# Revit family: Civil_Drainage_ACO_StormBrixx wm
name_source: partatom
category: Pipe Accessories
revit_build: Autodesk Revit 2013 (Build: 20120221_2030(x64)
units: mm (PartAtom-declared; Revit-internal decimal feet)

## types (2) — shared parameters
Assembly Code = D2090300
Con A Out = 128 mm
Con B Out = 128 mm
Conection IN Dia = 225 mm  [stored 0.738189 ft]
Connection IN Rad = 113 mm
Connection OUT Dia = 225 mm  [stored 0.738189 ft]
Connection OUT Rad = 113 mm
Draindown Depth = 610 mm  [stored 2.00131 ft]
Draindown Width = 600 mm  [stored 1.9685 ft]
Exc A = 25.00°
Fax = +44 (0)1462 815895
Inlet Connection Pipe = Yes
Installation Guidelines = http://www.aco.co.uk
Keynote = R17:315
Layer Connector = Product Code: 314023, Material: Recycled Polypropylene, Weight: 0.1kg, Colour: Red, Dimensions: 100mm x 40mm x 46mm (L x W x H)
Location of ConIn = 900 mm  [stored 2.95276 ft]
Loss Method = K Coefficient from Table
Maintenance Guidelines = http://www.aco.co.uk
Manufacturer = ACO Technologies plc
Model = StormBrixx
Product Documentation = http://www.aco.co.uk
Product Website = www.stormbrixx.co.uk
Side Panel = Product Code: 314021, Material: Recycled Polypropylene, Weight: 1.6kg, Colour: Black, Dimensions: 580mm x 578mm x 35mm (L x W x H)
Tank Body = Product Code: 314020, Material: Recycled Polypropylene, Weight: 10kg, Colour: Black, Dimensions: 1200mm x 600mm x 305mm (L x W x H), Vertical compressive strength: 420 kN/m², Lateral compressive strength: 90 kN/m², Void Ratio: 95%
Telephone = +44 (0)1462 816666
Trap W = 600 mm  [stored 1.9685 ft]
URL = www.aco.co.uk
_current revision = 1
_distributed by = www.aco.co.uk
zero-valued in all types: Barcode, Cost, ExpectedLife, SerialNumber, TagNumber

## per-type parameters (varying)
| type | Description | MIC | Outlet Connection Pipe | Outlet Connection Side | SIC | Top Cover | Type Comments |
| Attenuation System Configuration | ACO StormBrixx Attenuation System, configured as Attenuation system | No | Yes | No | Yes | Product Code: 314022 (set of 4), Material: Recycled Polypropylene, Weight: 0.8kg (per set), Colour: Black, Dimensions: 550mm x550mm x 43mm (L x W x H) | Attenuation System |
| Infiltration System Configuration | ACO StormBrixx Auttenuation System, configured as Infiltration system | Yes | No | Yes | No | Product Code: 314022 (set of 4), Material: Recycled Polypropylene, Weight: 0.8kg (per set), Colour: Black, Dimensions: 550mm x 550mm x 43mm (L x W x H) | Inflitration System |

note: [stored X ft] marks values corroborated as IEEE doubles in the binary element streams (Revit-internal decimal feet)

## geometry (parser evidence)
native form markers: Blend x10, Sweep x6
no freeform markers — native parametric forms only
